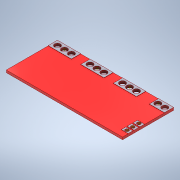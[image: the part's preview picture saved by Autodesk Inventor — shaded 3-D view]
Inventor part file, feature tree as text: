
AUTODESK INVENTOR PART (.ipt)
format: ipt  version: 2020 (Build 240168000, 168)  size: 246,272 bytes
history: native  units: mm
features: sketch x10, extrude x3, other x1
ambient origin geometry x8: Origin, YZ Plane, XZ Plane, XY Plane, X Axis, Y Axis, Z Axis, Center Point
bodies: Body1 (feature_tree)
feature tree (14):
  other  "Sólido1"
  extrude  "Extrusión1"  Depth=25.0mm
  extrude  "Extrusión2"  Depth=10.0mm
  extrude  "Extrusión3"  Depth=10.0mm
  sketch  "Boceto4"  dims[d9=4.0mm]
  sketch  "Boceto5"  dims[d10=10.0mm]
  sketch  "Boceto6"  dims[d11=4.0mm]
  sketch  "Boceto7"  dims[d12=6.5mm]
  sketch  "Boceto8"  dims[d13=4.0mm]
  sketch  "Boceto9"  dims[d14=3.0mm]
  sketch  "Boceto10"  dims[d15=2.0mm d20=0.1mm d21=0.0mm d22=0.0mm d23=0.0mm d24=14.0mm d25=14.0mm d27=0.0mm d28=2.0mm d29=3.0mm d30=2.0mm d31=0.5mm d32=0.5mm d33=2.5mm d34=2.5mm d35=2.5mm d36=2.0mm d37=2.0mm d38=3.0mm d39=2.0mm d40=3.0mm d41=2.0mm d42=2.5mm d43=2.5mm d44=2.5mm d45=3.0mm d46=3.0mm d47=2.0mm d48=2.5mm d49=2.5mm d50=2.5mm d51=3.0mm d52=3.0mm d53=2.5mm d54=2.5mm d56=3.0mm d58=1.7mm d59=2.0mm d60=1.5mm d61=1.5mm d62=1.5mm d63=1.5mm d64=5.1mm d65=0.0mm]
  sketch  "Boceto1"  dims[d2=11.0mm d3=25.0mm]
  sketch  "Boceto2"  dims[d4=1.0mm d5=0.0mm d6=10.0mm]
  sketch  "Boceto3"  dims[d7=4.0mm d8=10.0mm]
